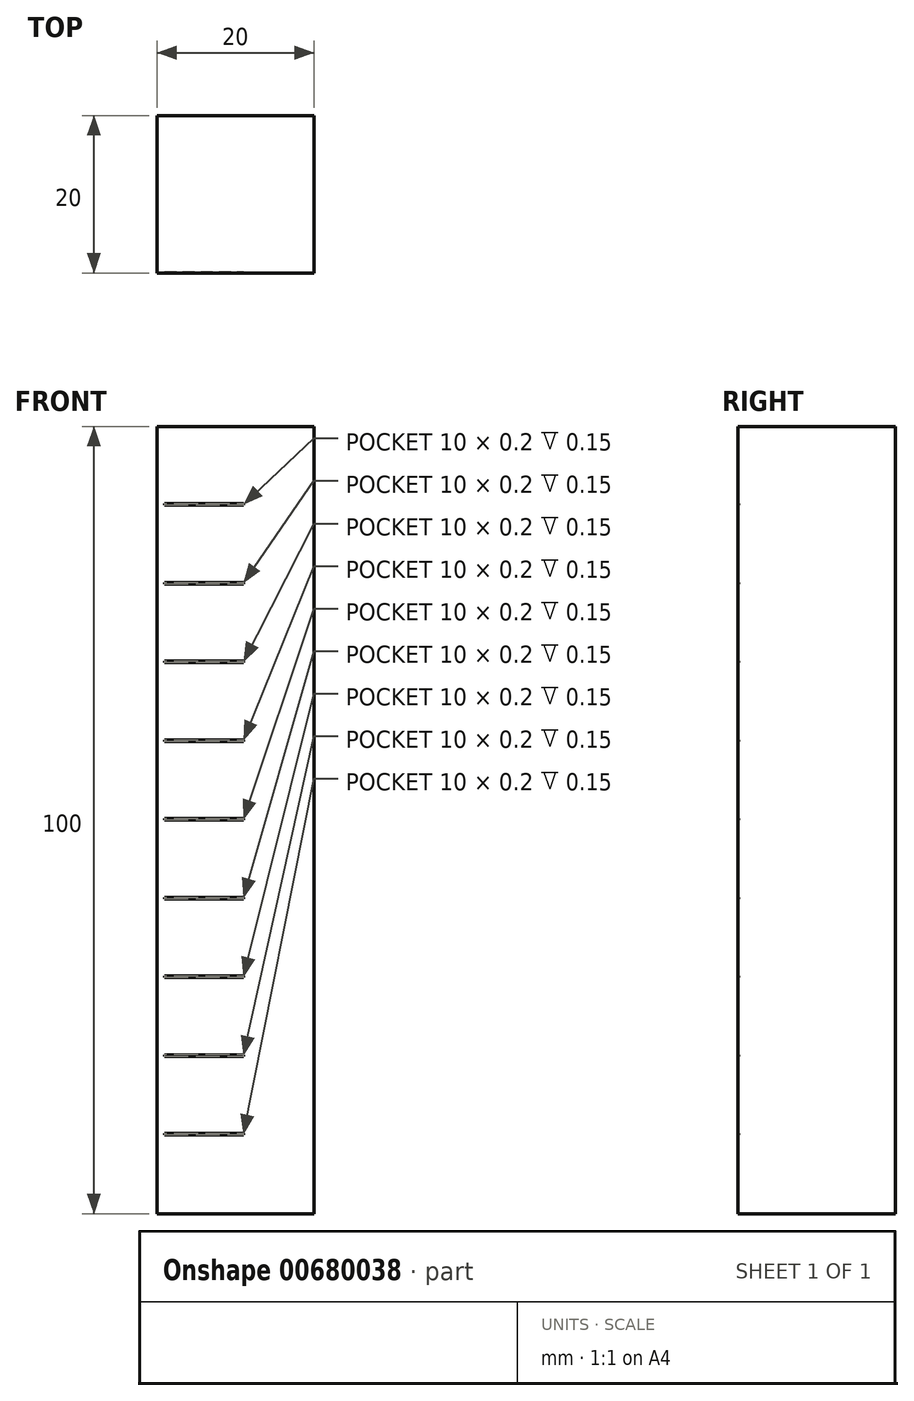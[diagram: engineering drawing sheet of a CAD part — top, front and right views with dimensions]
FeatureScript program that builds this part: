
annotation { "Feature Type Name" : "Feature", "Feature Type Description" : "" }
export const myFeature = defineFeature(function(context is Context, id is Id, definition is map)
    precondition{}
    {
        {
            var Q0;
            Q0=qCreatedBy(makeId("Top.planeOp"),FACE);
            var sketch = newSketch(context, id + "F0", { "sketchPlane" : qUnion([Q0])});
            skLineSegment(sketch, "E0.bottom", {"start": v(10, -10) * mm, "end": v(-10, -10) * mm});
            skLineSegment(sketch, "E0.top", {"start": v(10, 10) * mm, "end": v(-10, 10) * mm});
            skLineSegment(sketch, "E0.left", {"start": v(10, -10) * mm, "end": v(10, 10) * mm});
            skLineSegment(sketch, "E0.right", {"start": v(-10, -10) * mm, "end": v(-10, 10) * mm});
            skPoint(sketch, "E0.middle", {"position": v(0, 0) * mm});
            skSolve(sketch);
        }
        {
            var Q0;
            Q0=qSketchRegion(id+"F0",true);
            extrude(context, id + "F1", {"entities" : qUnion([Q0]), "depth" : 100 * mm, "offsetDistance" : 25 * mm});
        }
        {
            var Q0;
            Q0=makeQuery(id+"F1.opExtrude","SWEPT_FACE",FACE,{"disambiguationData":[OSD([sQuery(id+"F0.wireOp",EDGE,"E0.bottom")])]});
            var sketch = newSketch(context, id + "F2", { "sketchPlane" : qUnion([Q0])});
            skLineSegment(sketch, "E1.bottom", {"start": v(-9, 10.2) * mm, "end": v(1, 10.2) * mm});
            skLineSegment(sketch, "E1.top", {"start": v(-9, 10) * mm, "end": v(1, 10) * mm});
            skLineSegment(sketch, "E1.left", {"start": v(-9, 10.2) * mm, "end": v(-9, 10) * mm});
            skLineSegment(sketch, "E1.right", {"start": v(1, 10.2) * mm, "end": v(1, 10) * mm});
            skLineSegment(sketch, "E2.0.1.0", {"start": v(-9, 20) * mm, "end": v(1, 20) * mm});
            skLineSegment(sketch, "E2.0.1.1", {"start": v(-9, 20.2) * mm, "end": v(1, 20.2) * mm});
            skLineSegment(sketch, "E2.0.1.2", {"start": v(1, 20.2) * mm, "end": v(1, 20) * mm});
            skLineSegment(sketch, "E2.0.1.3", {"start": v(-9, 20.2) * mm, "end": v(-9, 20) * mm});
            skLineSegment(sketch, "E2.0.2.0", {"start": v(-9, 30) * mm, "end": v(1, 30) * mm});
            skLineSegment(sketch, "E2.0.2.1", {"start": v(-9, 30.2) * mm, "end": v(1, 30.2) * mm});
            skLineSegment(sketch, "E2.0.2.2", {"start": v(1, 30.2) * mm, "end": v(1, 30) * mm});
            skLineSegment(sketch, "E2.0.2.3", {"start": v(-9, 30.2) * mm, "end": v(-9, 30) * mm});
            skLineSegment(sketch, "E2.0.3.0", {"start": v(-9, 40) * mm, "end": v(1, 40) * mm});
            skLineSegment(sketch, "E2.0.3.1", {"start": v(-9, 40.2) * mm, "end": v(1, 40.2) * mm});
            skLineSegment(sketch, "E2.0.3.2", {"start": v(1, 40.2) * mm, "end": v(1, 40) * mm});
            skLineSegment(sketch, "E2.0.3.3", {"start": v(-9, 40.2) * mm, "end": v(-9, 40) * mm});
            skLineSegment(sketch, "E2.0.4.0", {"start": v(-9, 50) * mm, "end": v(1, 50) * mm});
            skLineSegment(sketch, "E2.0.4.1", {"start": v(-9, 50.2) * mm, "end": v(1, 50.2) * mm});
            skLineSegment(sketch, "E2.0.4.2", {"start": v(1, 50.2) * mm, "end": v(1, 50) * mm});
            skLineSegment(sketch, "E2.0.4.3", {"start": v(-9, 50.2) * mm, "end": v(-9, 50) * mm});
            skLineSegment(sketch, "E2.0.5.0", {"start": v(-9, 60) * mm, "end": v(1, 60) * mm});
            skLineSegment(sketch, "E2.0.5.1", {"start": v(-9, 60.2) * mm, "end": v(1, 60.2) * mm});
            skLineSegment(sketch, "E2.0.5.2", {"start": v(1, 60.2) * mm, "end": v(1, 60) * mm});
            skLineSegment(sketch, "E2.0.5.3", {"start": v(-9, 60.2) * mm, "end": v(-9, 60) * mm});
            skLineSegment(sketch, "E2.0.6.0", {"start": v(-9, 70) * mm, "end": v(1, 70) * mm});
            skLineSegment(sketch, "E2.0.6.1", {"start": v(-9, 70.2) * mm, "end": v(1, 70.2) * mm});
            skLineSegment(sketch, "E2.0.6.2", {"start": v(1, 70.2) * mm, "end": v(1, 70) * mm});
            skLineSegment(sketch, "E2.0.6.3", {"start": v(-9, 70.2) * mm, "end": v(-9, 70) * mm});
            skLineSegment(sketch, "E2.0.7.0", {"start": v(-9, 80) * mm, "end": v(1, 80) * mm});
            skLineSegment(sketch, "E2.0.7.1", {"start": v(-9, 80.2) * mm, "end": v(1, 80.2) * mm});
            skLineSegment(sketch, "E2.0.7.2", {"start": v(1, 80.2) * mm, "end": v(1, 80) * mm});
            skLineSegment(sketch, "E2.0.7.3", {"start": v(-9, 80.2) * mm, "end": v(-9, 80) * mm});
            skLineSegment(sketch, "E2.0.8.0", {"start": v(-9, 90) * mm, "end": v(1, 90) * mm});
            skLineSegment(sketch, "E2.0.8.1", {"start": v(-9, 90.2) * mm, "end": v(1, 90.2) * mm});
            skLineSegment(sketch, "E2.0.8.2", {"start": v(1, 90.2) * mm, "end": v(1, 90) * mm});
            skLineSegment(sketch, "E2.0.8.3", {"start": v(-9, 90.2) * mm, "end": v(-9, 90) * mm});
            skLineSegment(sketch, "E2.0.9.0", {"start": v(-9, 100) * mm, "end": v(1, 100) * mm});
            skLineSegment(sketch, "E2.0.9.1", {"start": v(-9, 100.2) * mm, "end": v(1, 100.2) * mm});
            skLineSegment(sketch, "E2.0.9.2", {"start": v(1, 100.2) * mm, "end": v(1, 100) * mm});
            skLineSegment(sketch, "E2.0.9.3", {"start": v(-9, 100.2) * mm, "end": v(-9, 100) * mm});
            skLineSegment(sketch, "E2.direction1", {"start": v(-9, 10) * mm, "end": v(6.4, 10) * mm, "construction": true});
            skLineSegment(sketch, "E2.direction2", {"start": v(-9, 10) * mm, "end": v(-9, 20) * mm, "construction": true});
            skSolve(sketch);
        }
        {
            var Q0;
            Q0=qSketchRegion(id+"F2",true);
            extrude(context, id + "F3", {"entities" : qUnion([Q0]), "operationType" : NewBodyOperationType.REMOVE, "oppositeDirection" : true, "depth" : .15 * mm, "offsetDistance" : 25 * mm});
        }
    });
